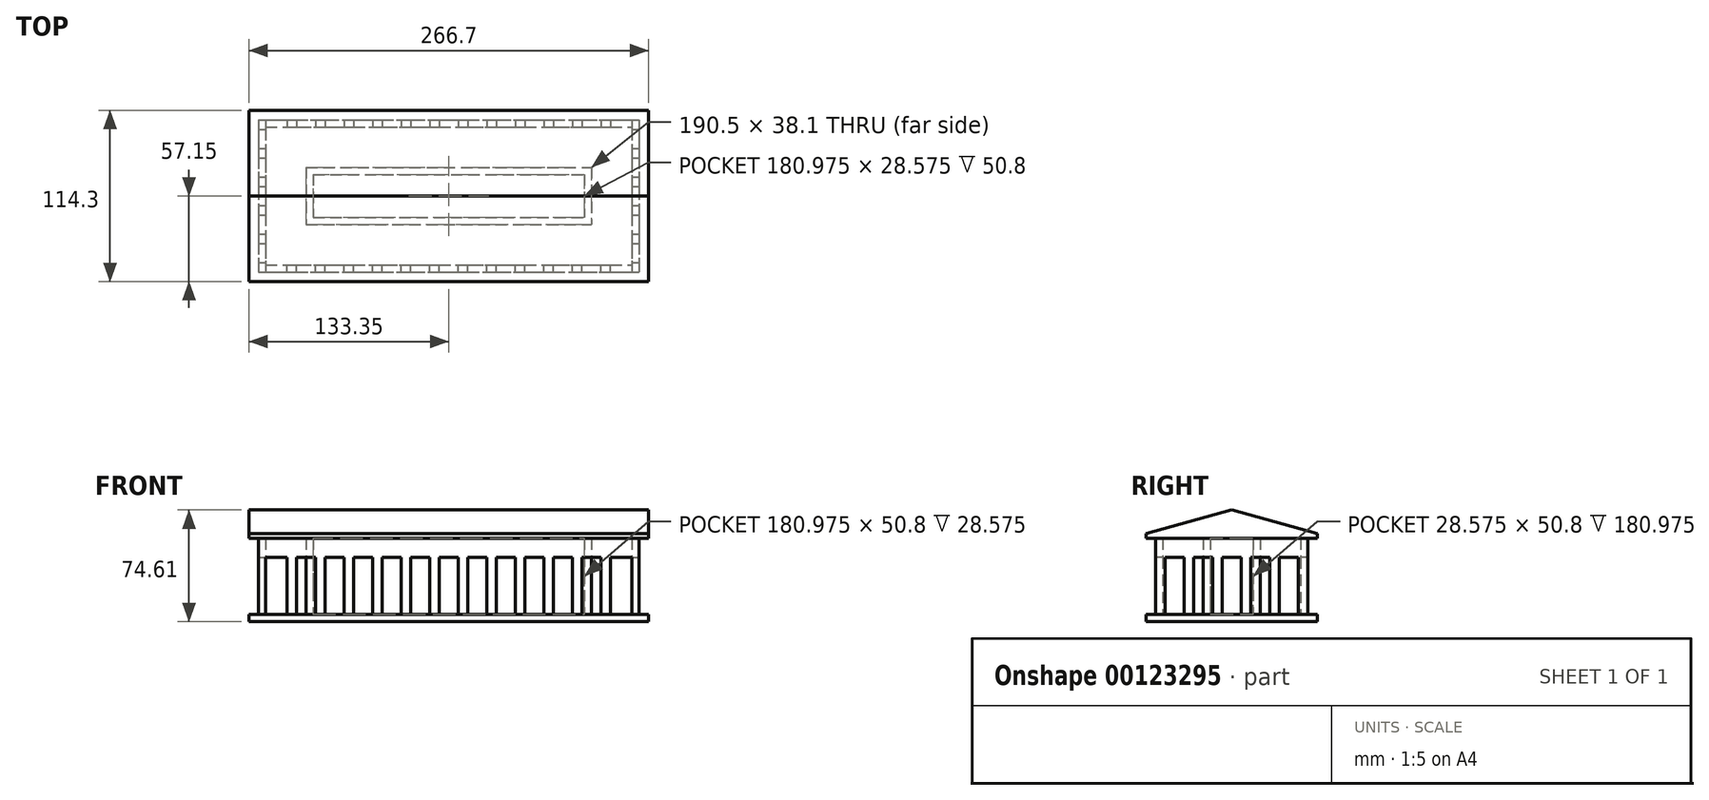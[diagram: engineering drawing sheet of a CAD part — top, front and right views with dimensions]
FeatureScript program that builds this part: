
annotation { "Feature Type Name" : "Feature", "Feature Type Description" : "" }
export const myFeature = defineFeature(function(context is Context, id is Id, definition is map)
    precondition{}
    {
        {
            var Q0;
            Q0=qCreatedBy(makeId("Top.planeOp"),FACE);
            var sketch = newSketch(context, id + "F0", { "sketchPlane" : qUnion([Q0])});
            skLineSegment(sketch, "E0.rect.bottom", {"start": v(-133.35, 57.15) * mm, "end": v(133.35, 57.15) * mm});
            skLineSegment(sketch, "E0.rect.top", {"start": v(-133.35, -57.15) * mm, "end": v(133.35, -57.15) * mm});
            skLineSegment(sketch, "E0.rect.left", {"start": v(-133.35, 57.15) * mm, "end": v(-133.35, -57.15) * mm});
            skLineSegment(sketch, "E0.rect.right", {"start": v(133.35, 57.15) * mm, "end": v(133.35, -57.15) * mm});
            skPoint(sketch, "E0.rect.middle", {"position": v(0, 0) * mm});
            skSolve(sketch);
        }
        {
            var Q0;
            Q0=qSketchRegion(id+"F0",true);
            extrude(context, id + "F1", {"entities" : qUnion([Q0]), "depth" : 4.76 * mm});
        }
        {
            var Q0;
            Q0=makeQuery(id+"F1.opExtrude","CAP_FACE",FACE,{"disambiguationData":[OSD([sQuery(id+"F0.wireOp",EDGE,"E0.rect.bottom"),sQuery(id+"F0.wireOp",EDGE,"E0.rect.top"),sQuery(id+"F0.wireOp",EDGE,"E0.rect.left"),sQuery(id+"F0.wireOp",EDGE,"E0.rect.right")])],"isStart":false});
            var sketch = newSketch(context, id + "F2", { "sketchPlane" : qUnion([Q0])});
            skLineSegment(sketch, "E1.bottom", {"start": v(-127, -44.45) * mm, "end": v(-122.24, -44.45) * mm});
            skLineSegment(sketch, "E1.top", {"start": v(-127, -50.8) * mm, "end": v(-122.24, -50.8) * mm});
            skLineSegment(sketch, "E1.left", {"start": v(-127, -44.45) * mm, "end": v(-127, -50.8) * mm});
            skLineSegment(sketch, "E1.right", {"start": v(-122.24, -44.45) * mm, "end": v(-122.24, -50.8) * mm});
            skLineSegment(sketch, "E2.0.1.0", {"start": v(-127, -25.4) * mm, "end": v(-122.24, -25.4) * mm});
            skLineSegment(sketch, "E2.0.1.1", {"start": v(-127, -31.75) * mm, "end": v(-122.24, -31.75) * mm});
            skLineSegment(sketch, "E2.0.1.2", {"start": v(-127, -25.4) * mm, "end": v(-127, -31.75) * mm});
            skLineSegment(sketch, "E2.0.1.3", {"start": v(-122.24, -25.4) * mm, "end": v(-122.24, -31.75) * mm});
            skLineSegment(sketch, "E2.0.2.0", {"start": v(-127, -6.35) * mm, "end": v(-122.24, -6.35) * mm});
            skLineSegment(sketch, "E2.0.2.1", {"start": v(-127, -12.7) * mm, "end": v(-122.24, -12.7) * mm});
            skLineSegment(sketch, "E2.0.2.2", {"start": v(-127, -6.35) * mm, "end": v(-127, -12.7) * mm});
            skLineSegment(sketch, "E2.0.2.3", {"start": v(-122.24, -6.35) * mm, "end": v(-122.24, -12.7) * mm});
            skLineSegment(sketch, "E2.0.3.0", {"start": v(-127, 12.7) * mm, "end": v(-122.24, 12.7) * mm});
            skLineSegment(sketch, "E2.0.3.1", {"start": v(-127, 6.35) * mm, "end": v(-122.24, 6.35) * mm});
            skLineSegment(sketch, "E2.0.3.2", {"start": v(-127, 12.7) * mm, "end": v(-127, 6.35) * mm});
            skLineSegment(sketch, "E2.0.3.3", {"start": v(-122.24, 12.7) * mm, "end": v(-122.24, 6.35) * mm});
            skLineSegment(sketch, "E2.0.4.0", {"start": v(-127, 31.75) * mm, "end": v(-122.24, 31.75) * mm});
            skLineSegment(sketch, "E2.0.4.1", {"start": v(-127, 25.4) * mm, "end": v(-122.24, 25.4) * mm});
            skLineSegment(sketch, "E2.0.4.2", {"start": v(-127, 31.75) * mm, "end": v(-127, 25.4) * mm});
            skLineSegment(sketch, "E2.0.4.3", {"start": v(-122.24, 31.75) * mm, "end": v(-122.24, 25.4) * mm});
            skLineSegment(sketch, "E2.0.5.0", {"start": v(-127, 50.8) * mm, "end": v(-122.24, 50.8) * mm});
            skLineSegment(sketch, "E2.0.5.1", {"start": v(-127, 44.45) * mm, "end": v(-122.24, 44.45) * mm});
            skLineSegment(sketch, "E2.0.5.2", {"start": v(-127, 50.8) * mm, "end": v(-127, 44.45) * mm});
            skLineSegment(sketch, "E2.0.5.3", {"start": v(-122.24, 50.8) * mm, "end": v(-122.24, 44.45) * mm});
            skLineSegment(sketch, "E2.direction1", {"start": v(-127, -44.45) * mm, "end": v(-101.6, -44.45) * mm, "construction": true});
            skLineSegment(sketch, "E2.direction2", {"start": v(-127, -44.45) * mm, "end": v(-127, -25.4) * mm, "construction": true});
            skLineSegment(sketch, "E3.direction1", {"start": v(-127, 50.8) * mm, "end": v(-107.95, 50.8) * mm, "construction": true});
            skLineSegment(sketch, "E4.0.13.0", {"start": v(122.24, 50.8) * mm, "end": v(127, 50.8) * mm});
            skLineSegment(sketch, "E4.3.13.0", {"start": v(127, 50.8) * mm, "end": v(127, 44.45) * mm});
            skLineSegment(sketch, "E4.6.13.0", {"start": v(122.24, 44.45) * mm, "end": v(127, 44.45) * mm});
            skLineSegment(sketch, "E4.9.13.0", {"start": v(122.24, 50.8) * mm, "end": v(122.24, 44.45) * mm});
            skLineSegment(sketch, "E5.13.0.0", {"start": v(127, -44.45) * mm, "end": v(127, -50.8) * mm});
            skLineSegment(sketch, "E5.13.0.1", {"start": v(122.24, -44.45) * mm, "end": v(127, -44.45) * mm});
            skLineSegment(sketch, "E5.13.0.2", {"start": v(122.24, -44.45) * mm, "end": v(122.24, -50.8) * mm});
            skLineSegment(sketch, "E5.13.0.3", {"start": v(122.24, -50.8) * mm, "end": v(127, -50.8) * mm});
            skLineSegment(sketch, "E5.direction1", {"start": v(-122.24, -50.8) * mm, "end": v(-103.19, -50.8) * mm, "construction": true});
            skLineSegment(sketch, "E6.0.1.0", {"start": v(122.24, 31.75) * mm, "end": v(127, 31.75) * mm});
            skLineSegment(sketch, "E6.0.1.1", {"start": v(122.24, 25.4) * mm, "end": v(127, 25.4) * mm});
            skLineSegment(sketch, "E6.0.1.2", {"start": v(127, 31.75) * mm, "end": v(127, 25.4) * mm});
            skLineSegment(sketch, "E6.0.1.3", {"start": v(122.24, 31.75) * mm, "end": v(122.24, 25.4) * mm});
            skLineSegment(sketch, "E6.0.2.0", {"start": v(122.24, 12.7) * mm, "end": v(127, 12.7) * mm});
            skLineSegment(sketch, "E6.0.2.1", {"start": v(122.24, 6.35) * mm, "end": v(127, 6.35) * mm});
            skLineSegment(sketch, "E6.0.2.2", {"start": v(127, 12.7) * mm, "end": v(127, 6.35) * mm});
            skLineSegment(sketch, "E6.0.2.3", {"start": v(122.24, 12.7) * mm, "end": v(122.24, 6.35) * mm});
            skLineSegment(sketch, "E6.0.3.0", {"start": v(122.24, -6.35) * mm, "end": v(127, -6.35) * mm});
            skLineSegment(sketch, "E6.0.3.1", {"start": v(122.24, -12.7) * mm, "end": v(127, -12.7) * mm});
            skLineSegment(sketch, "E6.0.3.2", {"start": v(127, -6.35) * mm, "end": v(127, -12.7) * mm});
            skLineSegment(sketch, "E6.0.3.3", {"start": v(122.24, -6.35) * mm, "end": v(122.24, -12.7) * mm});
            skLineSegment(sketch, "E6.0.4.0", {"start": v(122.24, -25.4) * mm, "end": v(127, -25.4) * mm});
            skLineSegment(sketch, "E6.0.4.1", {"start": v(122.24, -31.75) * mm, "end": v(127, -31.75) * mm});
            skLineSegment(sketch, "E6.0.4.2", {"start": v(127, -25.4) * mm, "end": v(127, -31.75) * mm});
            skLineSegment(sketch, "E6.0.4.3", {"start": v(122.24, -25.4) * mm, "end": v(122.24, -31.75) * mm});
            skLineSegment(sketch, "E6.direction1", {"start": v(122.24, 50.8) * mm, "end": v(96.84, 50.8) * mm, "construction": true});
            skLineSegment(sketch, "E6.direction2", {"start": v(122.24, 50.8) * mm, "end": v(122.24, 31.75) * mm, "construction": true});
            skLineSegment(sketch, "E7.bottom", {"start": v(-107.95, 50.8) * mm, "end": v(-101.6, 50.8) * mm});
            skLineSegment(sketch, "E7.top", {"start": v(-107.95, 46.04) * mm, "end": v(-101.6, 46.04) * mm});
            skLineSegment(sketch, "E7.left", {"start": v(-107.95, 50.8) * mm, "end": v(-107.95, 46.04) * mm});
            skLineSegment(sketch, "E7.right", {"start": v(-101.6, 50.8) * mm, "end": v(-101.6, 46.04) * mm});
            skLineSegment(sketch, "E8.1.0.0", {"start": v(-82.55, 50.8) * mm, "end": v(-82.55, 46.04) * mm});
            skLineSegment(sketch, "E8.1.0.1", {"start": v(-88.9, 50.8) * mm, "end": v(-82.55, 50.8) * mm});
            skLineSegment(sketch, "E8.1.0.2", {"start": v(-88.9, 50.8) * mm, "end": v(-88.9, 46.04) * mm});
            skLineSegment(sketch, "E8.1.0.3", {"start": v(-88.9, 46.04) * mm, "end": v(-82.55, 46.04) * mm});
            skLineSegment(sketch, "E8.2.0.0", {"start": v(-63.5, 50.8) * mm, "end": v(-63.5, 46.04) * mm});
            skLineSegment(sketch, "E8.2.0.1", {"start": v(-69.85, 50.8) * mm, "end": v(-63.5, 50.8) * mm});
            skLineSegment(sketch, "E8.2.0.2", {"start": v(-69.85, 50.8) * mm, "end": v(-69.85, 46.04) * mm});
            skLineSegment(sketch, "E8.2.0.3", {"start": v(-69.85, 46.04) * mm, "end": v(-63.5, 46.04) * mm});
            skLineSegment(sketch, "E8.3.0.0", {"start": v(-44.45, 50.8) * mm, "end": v(-44.45, 46.04) * mm});
            skLineSegment(sketch, "E8.3.0.1", {"start": v(-50.8, 50.8) * mm, "end": v(-44.45, 50.8) * mm});
            skLineSegment(sketch, "E8.3.0.2", {"start": v(-50.8, 50.8) * mm, "end": v(-50.8, 46.04) * mm});
            skLineSegment(sketch, "E8.3.0.3", {"start": v(-50.8, 46.04) * mm, "end": v(-44.45, 46.04) * mm});
            skLineSegment(sketch, "E8.4.0.0", {"start": v(-25.4, 50.8) * mm, "end": v(-25.4, 46.04) * mm});
            skLineSegment(sketch, "E8.4.0.1", {"start": v(-31.75, 50.8) * mm, "end": v(-25.4, 50.8) * mm});
            skLineSegment(sketch, "E8.4.0.2", {"start": v(-31.75, 50.8) * mm, "end": v(-31.75, 46.04) * mm});
            skLineSegment(sketch, "E8.4.0.3", {"start": v(-31.75, 46.04) * mm, "end": v(-25.4, 46.04) * mm});
            skLineSegment(sketch, "E8.5.0.0", {"start": v(-6.35, 50.8) * mm, "end": v(-6.35, 46.04) * mm});
            skLineSegment(sketch, "E8.5.0.1", {"start": v(-12.7, 50.8) * mm, "end": v(-6.35, 50.8) * mm});
            skLineSegment(sketch, "E8.5.0.2", {"start": v(-12.7, 50.8) * mm, "end": v(-12.7, 46.04) * mm});
            skLineSegment(sketch, "E8.5.0.3", {"start": v(-12.7, 46.04) * mm, "end": v(-6.35, 46.04) * mm});
            skLineSegment(sketch, "E8.6.0.0", {"start": v(12.7, 50.8) * mm, "end": v(12.7, 46.04) * mm});
            skLineSegment(sketch, "E8.6.0.1", {"start": v(6.35, 50.8) * mm, "end": v(12.7, 50.8) * mm});
            skLineSegment(sketch, "E8.6.0.2", {"start": v(6.35, 50.8) * mm, "end": v(6.35, 46.04) * mm});
            skLineSegment(sketch, "E8.6.0.3", {"start": v(6.35, 46.04) * mm, "end": v(12.7, 46.04) * mm});
            skLineSegment(sketch, "E8.7.0.0", {"start": v(31.75, 50.8) * mm, "end": v(31.75, 46.04) * mm});
            skLineSegment(sketch, "E8.7.0.1", {"start": v(25.4, 50.8) * mm, "end": v(31.75, 50.8) * mm});
            skLineSegment(sketch, "E8.7.0.2", {"start": v(25.4, 50.8) * mm, "end": v(25.4, 46.04) * mm});
            skLineSegment(sketch, "E8.7.0.3", {"start": v(25.4, 46.04) * mm, "end": v(31.75, 46.04) * mm});
            skLineSegment(sketch, "E8.8.0.0", {"start": v(50.8, 50.8) * mm, "end": v(50.8, 46.04) * mm});
            skLineSegment(sketch, "E8.8.0.1", {"start": v(44.45, 50.8) * mm, "end": v(50.8, 50.8) * mm});
            skLineSegment(sketch, "E8.8.0.2", {"start": v(44.45, 50.8) * mm, "end": v(44.45, 46.04) * mm});
            skLineSegment(sketch, "E8.8.0.3", {"start": v(44.45, 46.04) * mm, "end": v(50.8, 46.04) * mm});
            skLineSegment(sketch, "E8.9.0.0", {"start": v(69.85, 50.8) * mm, "end": v(69.85, 46.04) * mm});
            skLineSegment(sketch, "E8.9.0.1", {"start": v(63.5, 50.8) * mm, "end": v(69.85, 50.8) * mm});
            skLineSegment(sketch, "E8.9.0.2", {"start": v(63.5, 50.8) * mm, "end": v(63.5, 46.04) * mm});
            skLineSegment(sketch, "E8.9.0.3", {"start": v(63.5, 46.04) * mm, "end": v(69.85, 46.04) * mm});
            skLineSegment(sketch, "E8.10.0.0", {"start": v(88.9, 50.8) * mm, "end": v(88.9, 46.04) * mm});
            skLineSegment(sketch, "E8.10.0.1", {"start": v(82.55, 50.8) * mm, "end": v(88.9, 50.8) * mm});
            skLineSegment(sketch, "E8.10.0.2", {"start": v(82.55, 50.8) * mm, "end": v(82.55, 46.04) * mm});
            skLineSegment(sketch, "E8.10.0.3", {"start": v(82.55, 46.04) * mm, "end": v(88.9, 46.04) * mm});
            skLineSegment(sketch, "E8.11.0.0", {"start": v(107.95, 50.8) * mm, "end": v(107.95, 46.04) * mm});
            skLineSegment(sketch, "E8.11.0.1", {"start": v(101.6, 50.8) * mm, "end": v(107.95, 50.8) * mm});
            skLineSegment(sketch, "E8.11.0.2", {"start": v(101.6, 50.8) * mm, "end": v(101.6, 46.04) * mm});
            skLineSegment(sketch, "E8.11.0.3", {"start": v(101.6, 46.04) * mm, "end": v(107.95, 46.04) * mm});
            skLineSegment(sketch, "E8.direction1", {"start": v(-101.6, 46.04) * mm, "end": v(-82.55, 46.04) * mm, "construction": true});
            skLineSegment(sketch, "E9", {"start": v(0, 0) * mm, "end": v(-133.35, 0) * mm, "construction": true});
            skLineSegment(sketch, "E10", {"start": v(-133.35, 0) * mm, "end": v(133.35, 0) * mm, "construction": true});
            skLineSegment(sketch, "E11.MirrorCS", {"start": v(-69.85, -50.8) * mm, "end": v(-63.5, -50.8) * mm});
            skLineSegment(sketch, "E12.MirrorCS", {"start": v(101.6, -50.8) * mm, "end": v(101.6, -46.04) * mm});
            skLineSegment(sketch, "E13.MirrorCS", {"start": v(63.5, -50.8) * mm, "end": v(69.85, -50.8) * mm});
            skLineSegment(sketch, "E14.MirrorCS", {"start": v(-50.8, -50.8) * mm, "end": v(-50.8, -46.04) * mm});
            skLineSegment(sketch, "E15.MirrorCS", {"start": v(44.45, -50.8) * mm, "end": v(50.8, -50.8) * mm});
            skLineSegment(sketch, "E16.MirrorCS", {"start": v(-12.7, -46.04) * mm, "end": v(-6.35, -46.04) * mm});
            skLineSegment(sketch, "E17.MirrorCS", {"start": v(82.55, -50.8) * mm, "end": v(88.9, -50.8) * mm});
            skLineSegment(sketch, "E18.MirrorCS", {"start": v(63.5, -50.8) * mm, "end": v(63.5, -46.04) * mm});
            skLineSegment(sketch, "E19.MirrorCS", {"start": v(-69.85, -46.04) * mm, "end": v(-63.5, -46.04) * mm});
            skLineSegment(sketch, "E20.MirrorCS", {"start": v(6.35, -46.04) * mm, "end": v(12.7, -46.04) * mm});
            skLineSegment(sketch, "E21.MirrorCS", {"start": v(-69.85, -50.8) * mm, "end": v(-69.85, -46.04) * mm});
            skLineSegment(sketch, "E22.MirrorCS", {"start": v(-31.75, -50.8) * mm, "end": v(-31.75, -46.04) * mm});
            skLineSegment(sketch, "E23.MirrorCS", {"start": v(-107.95, -50.8) * mm, "end": v(-107.95, -46.04) * mm});
            skLineSegment(sketch, "E24.MirrorCS", {"start": v(44.45, -50.8) * mm, "end": v(44.45, -46.04) * mm});
            skLineSegment(sketch, "E25.MirrorCS", {"start": v(-88.9, -50.8) * mm, "end": v(-88.9, -46.04) * mm});
            skLineSegment(sketch, "E26.MirrorCS", {"start": v(101.6, -50.8) * mm, "end": v(107.95, -50.8) * mm});
            skLineSegment(sketch, "E27.MirrorCS", {"start": v(-88.9, -50.8) * mm, "end": v(-82.55, -50.8) * mm});
            skLineSegment(sketch, "E28.MirrorCS", {"start": v(107.95, -50.8) * mm, "end": v(107.95, -46.04) * mm});
            skLineSegment(sketch, "E29.MirrorCS", {"start": v(-44.45, -50.8) * mm, "end": v(-44.45, -46.04) * mm});
            skLineSegment(sketch, "E30.MirrorCS", {"start": v(25.4, -50.8) * mm, "end": v(25.4, -46.04) * mm});
            skLineSegment(sketch, "E31.MirrorCS", {"start": v(88.9, -50.8) * mm, "end": v(88.9, -46.04) * mm});
            skLineSegment(sketch, "E32.MirrorCS", {"start": v(31.75, -50.8) * mm, "end": v(31.75, -46.04) * mm});
            skLineSegment(sketch, "E33.MirrorCS", {"start": v(6.35, -50.8) * mm, "end": v(12.7, -50.8) * mm});
            skLineSegment(sketch, "E34.MirrorCS", {"start": v(63.5, -46.04) * mm, "end": v(69.85, -46.04) * mm});
            skLineSegment(sketch, "E35.MirrorCS", {"start": v(6.35, -50.8) * mm, "end": v(6.35, -46.04) * mm});
            skLineSegment(sketch, "E36.MirrorCS", {"start": v(-12.7, -50.8) * mm, "end": v(-12.7, -46.04) * mm});
            skLineSegment(sketch, "E37.MirrorCS", {"start": v(82.55, -50.8) * mm, "end": v(82.55, -46.04) * mm});
            skLineSegment(sketch, "E38.MirrorCS", {"start": v(-50.8, -50.8) * mm, "end": v(-44.45, -50.8) * mm});
            skLineSegment(sketch, "E39.MirrorCS", {"start": v(25.4, -50.8) * mm, "end": v(31.75, -50.8) * mm});
            skLineSegment(sketch, "E40.MirrorCS", {"start": v(-12.7, -50.8) * mm, "end": v(-6.35, -50.8) * mm});
            skLineSegment(sketch, "E41.MirrorCS", {"start": v(69.85, -50.8) * mm, "end": v(69.85, -46.04) * mm});
            skLineSegment(sketch, "E42.MirrorCS", {"start": v(101.6, -46.04) * mm, "end": v(107.95, -46.04) * mm});
            skLineSegment(sketch, "E43.MirrorCS", {"start": v(-50.8, -46.04) * mm, "end": v(-44.45, -46.04) * mm});
            skLineSegment(sketch, "E44.MirrorCS", {"start": v(25.4, -46.04) * mm, "end": v(31.75, -46.04) * mm});
            skLineSegment(sketch, "E45.MirrorCS", {"start": v(-88.9, -46.04) * mm, "end": v(-82.55, -46.04) * mm});
            skLineSegment(sketch, "E46.MirrorCS", {"start": v(-101.6, -50.8) * mm, "end": v(-101.6, -46.04) * mm});
            skLineSegment(sketch, "E47.MirrorCS", {"start": v(50.8, -50.8) * mm, "end": v(50.8, -46.04) * mm});
            skLineSegment(sketch, "E48.MirrorCS", {"start": v(44.45, -46.04) * mm, "end": v(50.8, -46.04) * mm});
            skLineSegment(sketch, "E49.MirrorCS", {"start": v(-107.95, -50.8) * mm, "end": v(-101.6, -50.8) * mm});
            skLineSegment(sketch, "E50.MirrorCS", {"start": v(-25.4, -50.8) * mm, "end": v(-25.4, -46.04) * mm});
            skLineSegment(sketch, "E51.MirrorCS", {"start": v(-31.75, -46.04) * mm, "end": v(-25.4, -46.04) * mm});
            skLineSegment(sketch, "E52.MirrorCS", {"start": v(-82.55, -50.8) * mm, "end": v(-82.55, -46.04) * mm});
            skLineSegment(sketch, "E53.MirrorCS", {"start": v(-6.35, -50.8) * mm, "end": v(-6.35, -46.04) * mm});
            skLineSegment(sketch, "E54.MirrorCS", {"start": v(-31.75, -50.8) * mm, "end": v(-25.4, -50.8) * mm});
            skLineSegment(sketch, "E55.MirrorCS", {"start": v(-107.95, -46.04) * mm, "end": v(-101.6, -46.04) * mm});
            skLineSegment(sketch, "E56.MirrorCS", {"start": v(12.7, -50.8) * mm, "end": v(12.7, -46.04) * mm});
            skLineSegment(sketch, "E57.MirrorCS", {"start": v(-63.5, -50.8) * mm, "end": v(-63.5, -46.04) * mm});
            skLineSegment(sketch, "E58.MirrorCS", {"start": v(82.55, -46.04) * mm, "end": v(88.9, -46.04) * mm});
            skLineSegment(sketch, "E59.MirrorCS", {"start": v(-101.6, -46.04) * mm, "end": v(-82.55, -46.04) * mm});
            skSolve(sketch);
        }
        {
            var Q0;
            Q0=makeQuery(id+"F2.imprint","IMPRINT",FACE,{"disambiguationData":[TD([[makeQuery(id+"F2.imprint","IMPRINT",EDGE,{"derivedFrom":sQuery(id+"F2.wireOp",EDGE,"E1.bottom")}),-1.0]])]});
            var Q1;
            Q1=makeQuery(id+"F2.imprint","IMPRINT",FACE,{"disambiguationData":[TD([[makeQuery(id+"F2.imprint","IMPRINT",EDGE,{"derivedFrom":sQuery(id+"F2.wireOp",EDGE,"E2.0.2.0")}),-1.0]])]});
            var Q2;
            Q2=makeQuery(id+"F2.imprint","IMPRINT",FACE,{"disambiguationData":[TD([[makeQuery(id+"F2.imprint","IMPRINT",EDGE,{"derivedFrom":sQuery(id+"F2.wireOp",EDGE,"E2.0.3.0")}),-1.0]])]});
            var Q3;
            Q3=makeQuery(id+"F2.imprint","IMPRINT",FACE,{"disambiguationData":[TD([[makeQuery(id+"F2.imprint","IMPRINT",EDGE,{"derivedFrom":sQuery(id+"F2.wireOp",EDGE,"E2.0.4.0")}),-1.0]])]});
            var Q4;
            Q4=makeQuery(id+"F2.imprint","IMPRINT",FACE,{"disambiguationData":[TD([[makeQuery(id+"F2.imprint","IMPRINT",EDGE,{"derivedFrom":sQuery(id+"F2.wireOp",EDGE,"E2.0.5.0")}),-1.0]])]});
            var Q5;
            Q5=makeQuery(id+"F2.imprint","IMPRINT",FACE,{"disambiguationData":[TD([[makeQuery(id+"F2.imprint","IMPRINT",EDGE,{"derivedFrom":sQuery(id+"F2.wireOp",EDGE,"E4.0.13.0")}),-1.0]])]});
            var Q6;
            Q6=makeQuery(id+"F2.imprint","IMPRINT",FACE,{"disambiguationData":[TD([[makeQuery(id+"F2.imprint","IMPRINT",EDGE,{"derivedFrom":sQuery(id+"F2.wireOp",EDGE,"E5.13.0.0")}),-1.0]])]});
            var Q7;
            Q7=makeQuery(id+"F2.imprint","IMPRINT",FACE,{"disambiguationData":[TD([[makeQuery(id+"F2.imprint","IMPRINT",EDGE,{"derivedFrom":sQuery(id+"F2.wireOp",EDGE,"E6.0.1.0")}),-1.0]])]});
            var Q8;
            Q8=makeQuery(id+"F2.imprint","IMPRINT",FACE,{"disambiguationData":[TD([[makeQuery(id+"F2.imprint","IMPRINT",EDGE,{"derivedFrom":sQuery(id+"F2.wireOp",EDGE,"E6.0.2.0")}),-1.0]])]});
            var Q9;
            Q9=makeQuery(id+"F2.imprint","IMPRINT",FACE,{"disambiguationData":[TD([[makeQuery(id+"F2.imprint","IMPRINT",EDGE,{"derivedFrom":sQuery(id+"F2.wireOp",EDGE,"E6.0.3.0")}),-1.0]])]});
            var Q10;
            Q10=makeQuery(id+"F2.imprint","IMPRINT",FACE,{"disambiguationData":[TD([[makeQuery(id+"F2.imprint","IMPRINT",EDGE,{"derivedFrom":sQuery(id+"F2.wireOp",EDGE,"E6.0.4.0")}),-1.0]])]});
            var Q11;
            Q11=makeQuery(id+"F2.imprint","IMPRINT",FACE,{"disambiguationData":[TD([[makeQuery(id+"F2.imprint","IMPRINT",EDGE,{"derivedFrom":sQuery(id+"F2.wireOp",EDGE,"E7.bottom")}),-1.0]])]});
            var Q12;
            Q12=makeQuery(id+"F2.imprint","IMPRINT",FACE,{"disambiguationData":[TD([[makeQuery(id+"F2.imprint","IMPRINT",EDGE,{"derivedFrom":sQuery(id+"F2.wireOp",EDGE,"E8.1.0.0")}),-1.0]])]});
            var Q13;
            Q13=makeQuery(id+"F2.imprint","IMPRINT",FACE,{"disambiguationData":[TD([[makeQuery(id+"F2.imprint","IMPRINT",EDGE,{"derivedFrom":sQuery(id+"F2.wireOp",EDGE,"E8.2.0.0")}),-1.0]])]});
            var Q14;
            Q14=makeQuery(id+"F2.imprint","IMPRINT",FACE,{"disambiguationData":[TD([[makeQuery(id+"F2.imprint","IMPRINT",EDGE,{"derivedFrom":sQuery(id+"F2.wireOp",EDGE,"E8.3.0.0")}),-1.0]])]});
            var Q15;
            Q15=makeQuery(id+"F2.imprint","IMPRINT",FACE,{"disambiguationData":[TD([[makeQuery(id+"F2.imprint","IMPRINT",EDGE,{"derivedFrom":sQuery(id+"F2.wireOp",EDGE,"E8.4.0.0")}),-1.0]])]});
            var Q16;
            Q16=makeQuery(id+"F2.imprint","IMPRINT",FACE,{"disambiguationData":[TD([[makeQuery(id+"F2.imprint","IMPRINT",EDGE,{"derivedFrom":sQuery(id+"F2.wireOp",EDGE,"E8.5.0.0")}),-1.0]])]});
            var Q17;
            Q17=makeQuery(id+"F2.imprint","IMPRINT",FACE,{"disambiguationData":[TD([[makeQuery(id+"F2.imprint","IMPRINT",EDGE,{"derivedFrom":sQuery(id+"F2.wireOp",EDGE,"E8.6.0.0")}),-1.0]])]});
            var Q18;
            Q18=makeQuery(id+"F2.imprint","IMPRINT",FACE,{"disambiguationData":[TD([[makeQuery(id+"F2.imprint","IMPRINT",EDGE,{"derivedFrom":sQuery(id+"F2.wireOp",EDGE,"E8.7.0.0")}),-1.0]])]});
            var Q19;
            Q19=makeQuery(id+"F2.imprint","IMPRINT",FACE,{"disambiguationData":[TD([[makeQuery(id+"F2.imprint","IMPRINT",EDGE,{"derivedFrom":sQuery(id+"F2.wireOp",EDGE,"E8.8.0.0")}),-1.0]])]});
            var Q20;
            Q20=makeQuery(id+"F2.imprint","IMPRINT",FACE,{"disambiguationData":[TD([[makeQuery(id+"F2.imprint","IMPRINT",EDGE,{"derivedFrom":sQuery(id+"F2.wireOp",EDGE,"E8.9.0.0")}),-1.0]])]});
            var Q21;
            Q21=makeQuery(id+"F2.imprint","IMPRINT",FACE,{"disambiguationData":[TD([[makeQuery(id+"F2.imprint","IMPRINT",EDGE,{"derivedFrom":sQuery(id+"F2.wireOp",EDGE,"E8.10.0.0")}),-1.0]])]});
            var Q22;
            Q22=makeQuery(id+"F2.imprint","IMPRINT",FACE,{"disambiguationData":[TD([[makeQuery(id+"F2.imprint","IMPRINT",EDGE,{"derivedFrom":sQuery(id+"F2.wireOp",EDGE,"E8.11.0.0")}),-1.0]])]});
            var Q23;
            Q23=makeQuery(id+"F2.imprint","IMPRINT",FACE,{"disambiguationData":[TD([[makeQuery(id+"F2.imprint","IMPRINT",EDGE,{"derivedFrom":sQuery(id+"F2.wireOp",EDGE,"E2.0.1.0")}),-1.0]])]});
            var Q24;
            {var subQ2=sQuery(id+"F2.wireOp",EDGE,"E25.MirrorCS");Q24=makeQuery(id+"F2.imprint","IMPRINT",FACE,{"disambiguationData":[TD([[makeQuery(id+"F2.imprint","IMPRINT",EDGE,{"derivedFrom":subQ2}),-1.0]])]});}
            var Q25;
            Q25=makeQuery(id+"F2.imprint","IMPRINT",FACE,{"disambiguationData":[TD([[makeQuery(id+"F2.imprint","IMPRINT",EDGE,{"derivedFrom":sQuery(id+"F2.wireOp",EDGE,"E23.MirrorCS")}),-1.0]])]});
            var Q26;
            Q26=makeQuery(id+"F2.imprint","IMPRINT",FACE,{"disambiguationData":[TD([[makeQuery(id+"F2.imprint","IMPRINT",EDGE,{"derivedFrom":sQuery(id+"F2.wireOp",EDGE,"E11.MirrorCS")}),1.0]])]});
            var Q27;
            Q27=makeQuery(id+"F2.imprint","IMPRINT",FACE,{"disambiguationData":[TD([[makeQuery(id+"F2.imprint","IMPRINT",EDGE,{"derivedFrom":sQuery(id+"F2.wireOp",EDGE,"E14.MirrorCS")}),-1.0]])]});
            var Q28;
            Q28=makeQuery(id+"F2.imprint","IMPRINT",FACE,{"disambiguationData":[TD([[makeQuery(id+"F2.imprint","IMPRINT",EDGE,{"derivedFrom":sQuery(id+"F2.wireOp",EDGE,"E22.MirrorCS")}),-1.0]])]});
            var Q29;
            Q29=makeQuery(id+"F2.imprint","IMPRINT",FACE,{"disambiguationData":[TD([[makeQuery(id+"F2.imprint","IMPRINT",EDGE,{"derivedFrom":sQuery(id+"F2.wireOp",EDGE,"E16.MirrorCS")}),-1.0]])]});
            var Q30;
            Q30=makeQuery(id+"F2.imprint","IMPRINT",FACE,{"disambiguationData":[TD([[makeQuery(id+"F2.imprint","IMPRINT",EDGE,{"derivedFrom":sQuery(id+"F2.wireOp",EDGE,"E20.MirrorCS")}),-1.0]])]});
            var Q31;
            Q31=makeQuery(id+"F2.imprint","IMPRINT",FACE,{"disambiguationData":[TD([[makeQuery(id+"F2.imprint","IMPRINT",EDGE,{"derivedFrom":sQuery(id+"F2.wireOp",EDGE,"E30.MirrorCS")}),-1.0]])]});
            var Q32;
            Q32=makeQuery(id+"F2.imprint","IMPRINT",FACE,{"disambiguationData":[TD([[makeQuery(id+"F2.imprint","IMPRINT",EDGE,{"derivedFrom":sQuery(id+"F2.wireOp",EDGE,"E15.MirrorCS")}),1.0]])]});
            var Q33;
            Q33=makeQuery(id+"F2.imprint","IMPRINT",FACE,{"disambiguationData":[TD([[makeQuery(id+"F2.imprint","IMPRINT",EDGE,{"derivedFrom":sQuery(id+"F2.wireOp",EDGE,"E13.MirrorCS")}),1.0]])]});
            var Q34;
            Q34=makeQuery(id+"F2.imprint","IMPRINT",FACE,{"disambiguationData":[TD([[makeQuery(id+"F2.imprint","IMPRINT",EDGE,{"derivedFrom":sQuery(id+"F2.wireOp",EDGE,"E17.MirrorCS")}),1.0]])]});
            var Q35;
            Q35=makeQuery(id+"F2.imprint","IMPRINT",FACE,{"disambiguationData":[TD([[makeQuery(id+"F2.imprint","IMPRINT",EDGE,{"derivedFrom":sQuery(id+"F2.wireOp",EDGE,"E12.MirrorCS")}),-1.0]])]});
            var Q36;
            Q36=qSketchRegion(id+"F4",true);
            extrude(context, id + "F3", {"entities" : qUnion([Q0, Q1, Q2, Q3, Q4, Q5, Q6, Q7, Q8, Q9, Q10, Q11, Q12, Q13, Q14, Q15, Q16, Q17, Q18, Q19, Q20, Q21, Q22, Q23, Q24, Q25, Q26, Q27, Q28, Q29, Q30, Q31, Q32, Q33, Q34, Q35, Q36]), "operationType" : NewBodyOperationType.ADD, "depth" : 38.1 * mm});
        }
        {
            var Q0;
            Q0=makeQuery(id+"F2.imprint","IMPRINT",FACE,{"disambiguationData":[TD([[makeQuery(id+"F2.imprint","IMPRINT",EDGE,{"derivedFrom":sQuery(id+"F2.wireOp",EDGE,"E1.bottom")}),1.0]])]});
            var sketch = newSketch(context, id + "F4", { "sketchPlane" : qUnion([Q0])});
            skLineSegment(sketch, "E60.0", {"start": v(-95.25, 19.05) * mm, "end": v(95.25, 19.05) * mm});
            skLineSegment(sketch, "E60.1", {"start": v(-95.25, 19.05) * mm, "end": v(-95.25, -19.05) * mm});
            skLineSegment(sketch, "E60.2", {"start": v(-95.25, -19.05) * mm, "end": v(95.25, -19.05) * mm});
            skLineSegment(sketch, "E60.3", {"start": v(95.25, 19.05) * mm, "end": v(95.25, -19.05) * mm});
            skLineSegment(sketch, "E61.0", {"start": v(127, 50.8) * mm, "end": v(-127, 50.8) * mm});
            skLineSegment(sketch, "E61.1", {"start": v(127, -50.8) * mm, "end": v(127, 50.8) * mm});
            skLineSegment(sketch, "E61.2", {"start": v(-127, -50.8) * mm, "end": v(127, -50.8) * mm});
            skLineSegment(sketch, "E61.3", {"start": v(-127, 50.8) * mm, "end": v(-127, -50.8) * mm});
            skLineSegment(sketch, "E62.0", {"start": v(-90.49, -14.29) * mm, "end": v(90.49, -14.29) * mm});
            skLineSegment(sketch, "E62.1", {"start": v(-90.49, 14.29) * mm, "end": v(-90.49, -14.29) * mm});
            skLineSegment(sketch, "E62.2", {"start": v(-90.49, 14.29) * mm, "end": v(90.49, 14.29) * mm});
            skLineSegment(sketch, "E62.3", {"start": v(90.49, 14.29) * mm, "end": v(90.49, -14.29) * mm});
            skSolve(sketch);
        }
        {
            var Q0;
            Q0=makeQuery(id+"F4.imprint","IMPRINT",FACE,{"disambiguationData":[TD([[makeQuery(id+"F4.imprint","IMPRINT",EDGE,{"derivedFrom":sQuery(id+"F4.wireOp",EDGE,"E60.0")}),-1.0]])]});
            extrude(context, id + "F5", {"entities" : qUnion([Q0]), "operationType" : NewBodyOperationType.ADD, "depth" : 50.8 * mm});
        }
        {
            var Q0;
            Q0=makeQuery(id+"F3.opExtrude","CAP_FACE",FACE,{"disambiguationData":[OSD([sQuery(id+"F2.wireOp",EDGE,"E2.0.4.0"),sQuery(id+"F2.wireOp",EDGE,"E2.0.4.1"),sQuery(id+"F2.wireOp",EDGE,"E2.0.4.2"),sQuery(id+"F2.wireOp",EDGE,"E2.0.4.3")])],"isStart":false});
            var sketch = newSketch(context, id + "F6", { "sketchPlane" : qUnion([Q0])});
            skLineSegment(sketch, "E63.rect.bottom", {"start": v(-127, 50.8) * mm, "end": v(127, 50.8) * mm});
            skLineSegment(sketch, "E63.rect.top", {"start": v(-127, -50.8) * mm, "end": v(127, -50.8) * mm});
            skLineSegment(sketch, "E63.rect.left", {"start": v(-127, 50.8) * mm, "end": v(-127, -50.8) * mm});
            skLineSegment(sketch, "E63.rect.right", {"start": v(127, 50.8) * mm, "end": v(127, -50.8) * mm});
            skPoint(sketch, "E63.rect.middle", {"position": v(0, 0) * mm});
            skLineSegment(sketch, "E64.0", {"start": v(-122.24, 46.04) * mm, "end": v(122.24, 46.04) * mm});
            skLineSegment(sketch, "E64.1", {"start": v(-122.24, 46.04) * mm, "end": v(-122.24, -46.04) * mm});
            skLineSegment(sketch, "E64.2", {"start": v(-122.24, -46.04) * mm, "end": v(122.24, -46.04) * mm});
            skLineSegment(sketch, "E64.3", {"start": v(122.24, 46.04) * mm, "end": v(122.24, -46.04) * mm});
            skLineSegment(sketch, "E65.0", {"start": v(127, 50.8) * mm, "end": v(-127, 50.8) * mm});
            skLineSegment(sketch, "E65.1", {"start": v(127, -50.8) * mm, "end": v(127, 50.8) * mm});
            skSolve(sketch);
        }
        {
            var Q0;
            {var subQ4=sQuery(id+"F6.wireOp",EDGE,"E64.0");Q0=makeQuery(id+"F6.imprint","IMPRINT",FACE,{"disambiguationData":[TD([[makeQuery(id+"F6.imprint","IMPRINT",EDGE,{"derivedFrom":subQ4}),1.0]])]});}
            var Q1;
            {var subQ1=makeQuery(id+"F3.opExtrude","CAP_EDGE",EDGE,{"disambiguationData":[OSD([sQuery(id+"F2.wireOp",EDGE,"E2.0.4.0")])],"isStart":false});Q1=makeQuery(id+"F6.imprint","IMPRINT",FACE,{"disambiguationData":[TD([[makeQuery(id+"F6.imprint","IMPRINT",EDGE,{"derivedFrom":subQ1}),-1.0]])]});}
            extrude(context, id + "F7", {"entities" : qUnion([Q0, Q1]), "operationType" : NewBodyOperationType.ADD, "depth" : 12.7 * mm});
        }
        {
            var Q0;
            Q0=makeQuery(id+"F1.opExtrude","SWEPT_FACE",FACE,{"disambiguationData":[OSD([sQuery(id+"F0.wireOp",EDGE,"E0.rect.left")])]});
            var sketch = newSketch(context, id + "F8", { "sketchPlane" : qUnion([Q0])});
            skPoint(sketch, "E66.0", {"position": v(-50.8, 55.56) * mm});
            skPoint(sketch, "E67.0", {"position": v(50.8, 55.56) * mm});
            skLineSegment(sketch, "E68", {"start": v(-50.8, 55.56) * mm, "end": v(50.8, 55.56) * mm});
            skLineSegment(sketch, "E69", {"start": v(-50.8, 55.56) * mm, "end": v(-57.15, 55.56) * mm});
            skLineSegment(sketch, "E70", {"start": v(50.8, 55.56) * mm, "end": v(57.15, 55.56) * mm});
            skLineSegment(sketch, "E71", {"start": v(-57.15, 55.56) * mm, "end": v(-57.15, 58.74) * mm});
            skLineSegment(sketch, "E72", {"start": v(57.15, 55.56) * mm, "end": v(57.15, 58.74) * mm});
            skLineSegment(sketch, "E73", {"start": v(-57.15, 58.74) * mm, "end": v(0, 74.61) * mm});
            skLineSegment(sketch, "E74", {"start": v(0, 74.61) * mm, "end": v(57.15, 58.74) * mm});
            skSolve(sketch);
        }
        {
            var Q0;
            Q0=qSketchRegion(id+"F8",true);
            var Q1;
            Q1=makeQuery(id+"F1.opExtrude","SWEPT_FACE",FACE,{"disambiguationData":[OSD([sQuery(id+"F0.wireOp",EDGE,"E0.rect.right")])]});
            extrude(context, id + "F9", {"entities" : qUnion([Q0]), "operationType" : NewBodyOperationType.ADD, "endBound" : BoundingType.UP_TO_SURFACE, "oppositeDirection" : true, "endBoundEntityFace" : qUnion([Q1]), "depth" : 25.4 * mm});
        }
    });
